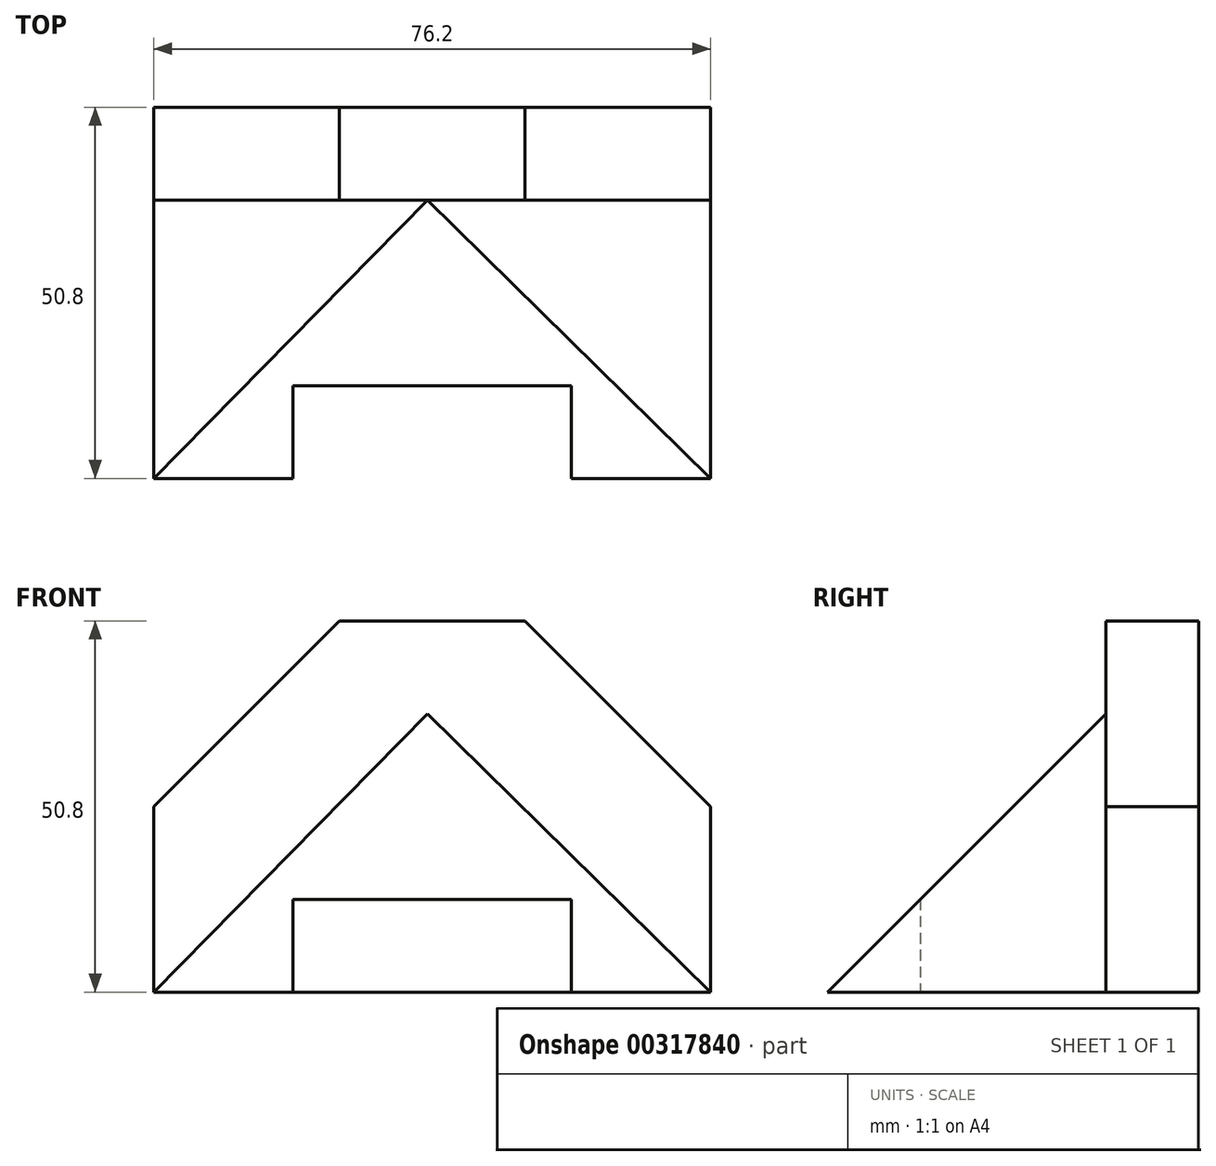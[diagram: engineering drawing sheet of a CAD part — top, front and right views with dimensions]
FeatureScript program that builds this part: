
annotation { "Feature Type Name" : "Feature", "Feature Type Description" : "" }
export const myFeature = defineFeature(function(context is Context, id is Id, definition is map)
    precondition{}
    {
        {
            var Q0;
            Q0=qCreatedBy(makeId("Front.planeOp"),FACE);
            var sketch = newSketch(context, id + "F0", { "sketchPlane" : qUnion([Q0])});
            skLineSegment(sketch, "E0.bottom", {"start": v(0, 0) * mm, "end": v(76.2, 0) * mm});
            skLineSegment(sketch, "E0.top", {"start": v(0, 50.8) * mm, "end": v(76.2, 50.8) * mm});
            skLineSegment(sketch, "E0.left", {"start": v(0, 0) * mm, "end": v(0, 50.8) * mm});
            skLineSegment(sketch, "E0.right", {"start": v(76.2, 0) * mm, "end": v(76.2, 50.8) * mm});
            skSolve(sketch);
        }
        {
            var Q0;
            Q0 = qSketchRegion(id + "F0", true);
            extrude(context, id + "F1", {"entities" : qUnion([Q0]), "depth" : 50.8 * mm});
        }
        {
            var Q0;
            Q0=makeQuery(id+"F1.opExtrude","CAP_FACE",FACE,{"disambiguationData":[OSD([sQuery(id+"F0.wireOp",EDGE,"E0.bottom"),sQuery(id+"F0.wireOp",EDGE,"E0.top"),sQuery(id+"F0.wireOp",EDGE,"E0.left"),sQuery(id+"F0.wireOp",EDGE,"E0.right")])],"isStart":false});
            var sketch = newSketch(context, id + "F2", { "sketchPlane" : qUnion([Q0])});
            skLineSegment(sketch, "E1", {"start": v(0, 25.4) * mm, "end": v(25.4, 50.8) * mm});
            skLineSegment(sketch, "E2", {"start": v(25.4, 50.8) * mm, "end": v(0, 50.8) * mm});
            skLineSegment(sketch, "E3", {"start": v(0, 50.8) * mm, "end": v(0, 25.4) * mm});
            skLineSegment(sketch, "E4", {"start": v(76.2, 50.8) * mm, "end": v(76.2, 25.4) * mm});
            skLineSegment(sketch, "E5", {"start": v(76.2, 25.4) * mm, "end": v(50.8, 50.8) * mm});
            skLineSegment(sketch, "E6", {"start": v(50.8, 50.8) * mm, "end": v(76.2, 50.8) * mm});
            skSolve(sketch);
        }
        {
            var Q0;
            Q0 = qSketchRegion(id + "F2", true);
            extrude(context, id + "F3", {"entities" : qUnion([Q0]), "operationType" : NewBodyOperationType.REMOVE, "endBound" : BoundingType.THROUGH_ALL, "oppositeDirection" : true, "depth" : 25.4 * mm});
        }
        {
            var Q0;
            Q0=makeQuery(id+"F1.opExtrude","SWEPT_FACE",FACE,{"disambiguationData":[OSD([sQuery(id+"F0.wireOp",EDGE,"E0.bottom")])]});
            var sketch = newSketch(context, id + "F4", { "sketchPlane" : qUnion([Q0])});
            skLineSegment(sketch, "E7.bottom", {"start": v(19.05, 50.8) * mm, "end": v(57.15, 50.8) * mm});
            skLineSegment(sketch, "E7.top", {"start": v(19.05, 38.1) * mm, "end": v(57.15, 38.1) * mm});
            skLineSegment(sketch, "E7.left", {"start": v(19.05, 50.8) * mm, "end": v(19.05, 38.1) * mm});
            skLineSegment(sketch, "E7.right", {"start": v(57.15, 50.8) * mm, "end": v(57.15, 38.1) * mm});
            skLineSegment(sketch, "E8", {"start": v(38.1, 50.8) * mm, "end": v(38.1, 62.85) * mm, "construction": true});
            skSolve(sketch);
        }
        {
            var Q0;
            Q0 = qSketchRegion(id + "F4", true);
            extrude(context, id + "F5", {"entities" : qUnion([Q0]), "operationType" : NewBodyOperationType.REMOVE, "endBound" : BoundingType.THROUGH_ALL, "oppositeDirection" : true, "depth" : 25.4 * mm});
        }
        {
            var Q0;
            {var subQ0=sQuery(id+"F0.wireOp",EDGE,"E0.bottom");var subQ1=sQuery(id+"F0.wireOp",EDGE,"E0.left");Q0=makeQuery(id+"F5.boolean.opBoolean","SPLIT",FACE,{"disambiguationData":[TD([makeQuery(id+"F1.opExtrude","SWEPT_FACE",FACE,{"disambiguationData":[OSD([subQ1])]})])],"derivedFrom":makeQuery(id+"F1.opExtrude","CAP_FACE",FACE,{"disambiguationData":[OSD([subQ0,sQuery(id+"F0.wireOp",EDGE,"E0.top"),subQ1,sQuery(id+"F0.wireOp",EDGE,"E0.right")])],"isStart":false})});}
            var sketch = newSketch(context, id + "F6", { "sketchPlane" : qUnion([Q0])});
            skLineSegment(sketch, "E9.0.3", {"start": v(57.15, 44.45) * mm, "end": v(50.8, 50.8) * mm});
            skLineSegment(sketch, "E9.0.4", {"start": v(50.8, 50.8) * mm, "end": v(25.4, 50.8) * mm});
            skLineSegment(sketch, "E9.0.5", {"start": v(25.4, 50.8) * mm, "end": v(19.05, 44.45) * mm});
            skLineSegment(sketch, "E10.0.0", {"start": v(76.2, 25.4) * mm, "end": v(57.15, 44.45) * mm});
            skLineSegment(sketch, "E11.0.1", {"start": v(19.05, 44.45) * mm, "end": v(0, 25.4) * mm});
            skPoint(sketch, "E11.0.3.start.orphan", {"position": v(0, 0) * mm});
            skPoint(sketch, "E10.0.3.start.orphan", {"position": v(76.2, 0) * mm});
            skLineSegment(sketch, "E12", {"start": v(37.46, 38.1) * mm, "end": v(0, 0) * mm});
            skLineSegment(sketch, "E13", {"start": v(37.46, 38.1) * mm, "end": v(76.2, 0) * mm});
            skLineSegment(sketch, "E14", {"start": v(0, 0) * mm, "end": v(0, 25.4) * mm});
            skLineSegment(sketch, "E15", {"start": v(76.2, 0) * mm, "end": v(76.2, 25.4) * mm});
            skSolve(sketch);
        }
        {
            var Q0;
            Q0 = qSketchRegion(id + "F6", true);
            extrude(context, id + "F7", {"entities" : qUnion([Q0]), "operationType" : NewBodyOperationType.REMOVE, "oppositeDirection" : true, "depth" : 38.1 * mm});
        }
        {
            var Q0;
            Q0=makeQuery(id+"F1.opExtrude","SWEPT_FACE",FACE,{"disambiguationData":[OSD([sQuery(id+"F0.wireOp",EDGE,"E0.right")])]});
            var sketch = newSketch(context, id + "F8", { "sketchPlane" : qUnion([Q0])});
            skLineSegment(sketch, "E16.0.4", {"start": v(-12.7, 38.1) * mm, "end": v(-38.1, 38.1) * mm});
            skLineSegment(sketch, "E17", {"start": v(-50.8, 0) * mm, "end": v(-12.7, 38.1) * mm});
            skPoint(sketch, "E16.0.2.end.orphan", {"position": v(-12.7, 0) * mm});
            skPoint(sketch, "E16.0.5.end.orphan", {"position": v(-38.1, 18.74) * mm});
            skPoint(sketch, "E16.0.1.start.orphan", {"position": v(-50.8, 18.74) * mm});
            skLineSegment(sketch, "E18", {"start": v(-50.8, 0) * mm, "end": v(-50.8, 28.34) * mm});
            skLineSegment(sketch, "E19", {"start": v(-50.8, 28.34) * mm, "end": v(-38.1, 38.1) * mm});
            skSolve(sketch);
        }
        {
            var Q0;
            Q0 = qSketchRegion(id + "F8", true);
            extrude(context, id + "F9", {"entities" : qUnion([Q0]), "operationType" : NewBodyOperationType.REMOVE, "endBound" : BoundingType.THROUGH_ALL, "oppositeDirection" : true, "depth" : 25.4 * mm});
        }
    });
